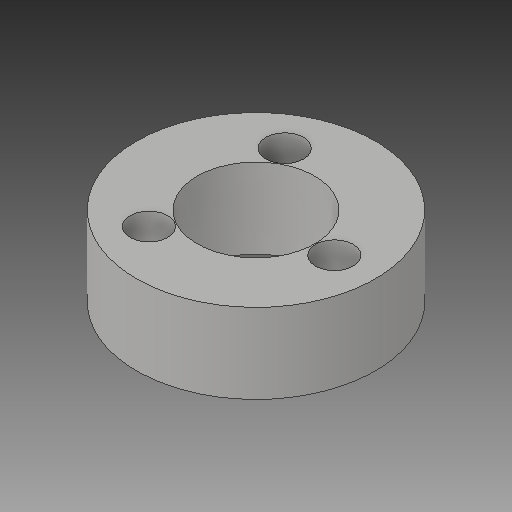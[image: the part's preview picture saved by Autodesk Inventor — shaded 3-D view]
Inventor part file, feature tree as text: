
AUTODESK INVENTOR PART (.ipt)
format: ipt  version: 2018 (Build 220112000, 112)  size: 102,912 bytes
history: native  units: in
note: dims shown in document units (in); Inventor stores cm internally (conversion verified against a paired STEP export)
features: extrude x2, sketch x2
ambient origin geometry x8: Origin, YZ Plane, XZ Plane, XY Plane, X Axis, Y Axis, Z Axis, Center Point
bodies: Solid1 (feature_tree)
feature tree (4):
  extrude  "Extrusion1"  Depth=1.5795in TaperAngle=360.0deg
  extrude  "Extrusion2"  [1 undecoded]
  sketch  "Sketch1"  dims[d5=1.5795in d6=0.0in d11=1.1811in d13=360.0deg]
  sketch  "Sketch2"  dims[d16=1.5795in d17=0.0in]
note: 1 required parameter value undecoded (feature->parameter linkage not recoverable at this tier; creation-order binding heuristic only, values carry confidence <= 0.55)
